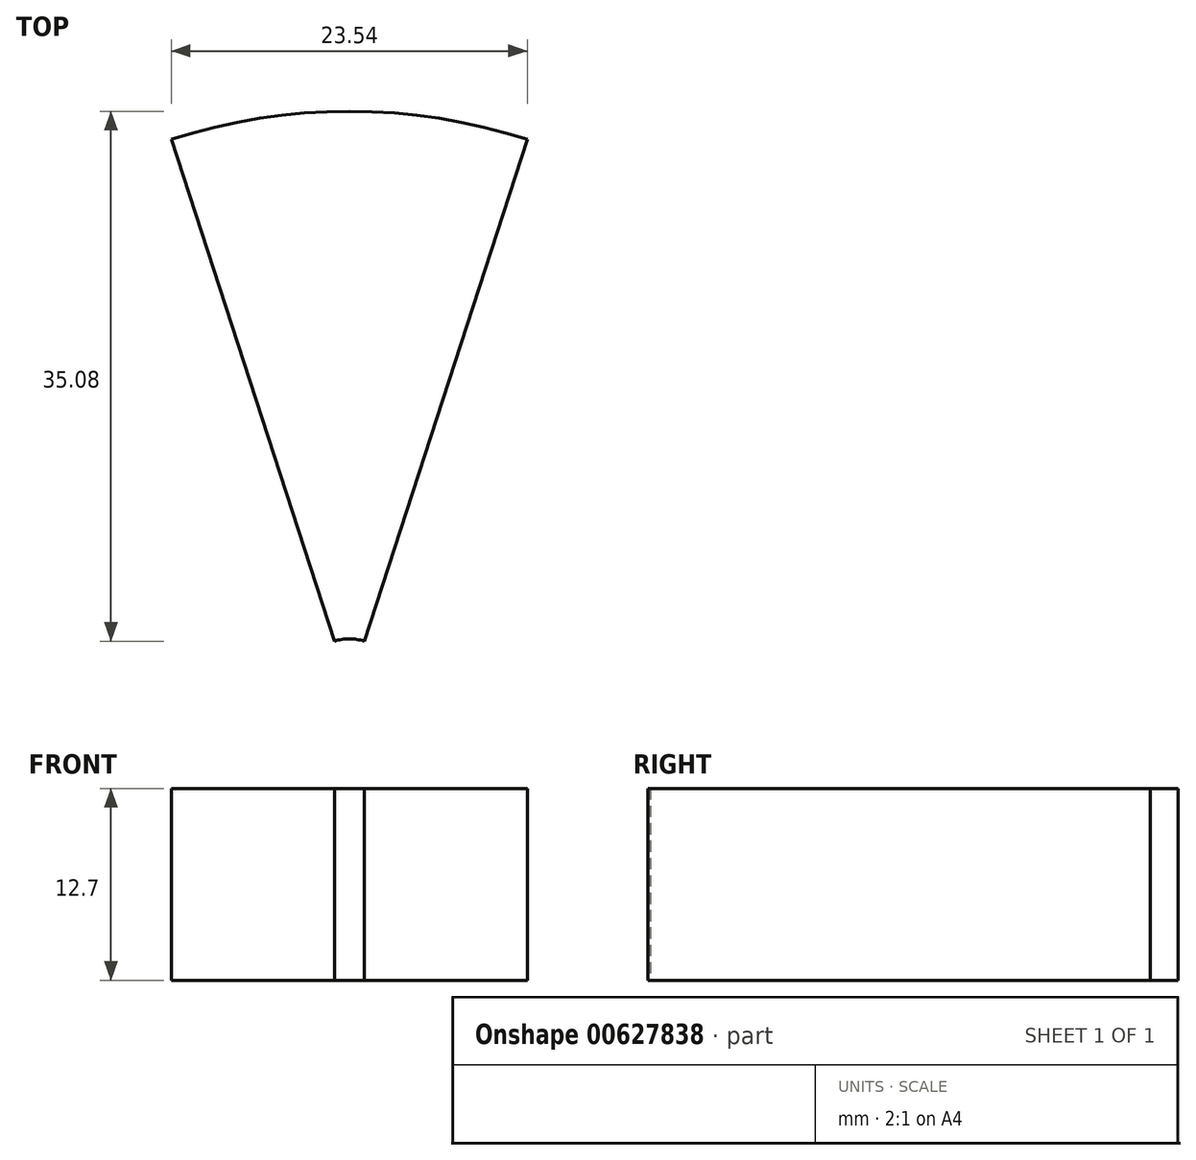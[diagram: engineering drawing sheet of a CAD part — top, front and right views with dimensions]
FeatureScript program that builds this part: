
annotation { "Feature Type Name" : "Feature", "Feature Type Description" : "" }
export const myFeature = defineFeature(function(context is Context, id is Id, definition is map)
    precondition{}
    {
        {
            var Q0;
            Q0=qCreatedBy(makeId("Top.planeOp"),FACE);
            var sketch = newSketch(context, id + "F0", { "sketchPlane" : qUnion([Q0])});
            skArc(sketch, "E0", {"start": v(11.77, 36.24) * mm, "mid": v(0, 38.1) * mm, "end": v(-11.77, 36.24) * mm});
            skLineSegment(sketch, "E1", {"start": v(0, 0) * mm, "end": v(0, 38.1) * mm, "construction": true});
            skLineSegment(sketch, "E2", {"start": v(0.98, 3.02) * mm, "end": v(11.77, 36.24) * mm});
            skLineSegment(sketch, "E3", {"start": v(-0.98, 3.02) * mm, "end": v(-11.77, 36.24) * mm});
            skArc(sketch, "E4", {"start": v(0.98, 3.02) * mm, "mid": v(0, 3.18) * mm, "end": v(-0.98, 3.02) * mm});
            skSolve(sketch);
        }
        {
            var Q0;
            Q0=makeQuery(id+"F0.imprint","IMPRINT",FACE,{"disambiguationData":[TD([[makeQuery(id+"F0.imprint","IMPRINT",EDGE,{"derivedFrom":sQuery(id+"F0.wireOp",EDGE,"E0")}),1.0]])]});
            extrude(context, id + "F1", {"entities" : qUnion([Q0]), "depth" : 12.7 * mm, "offsetDistance" : 25.4 * mm});
        }
    });
